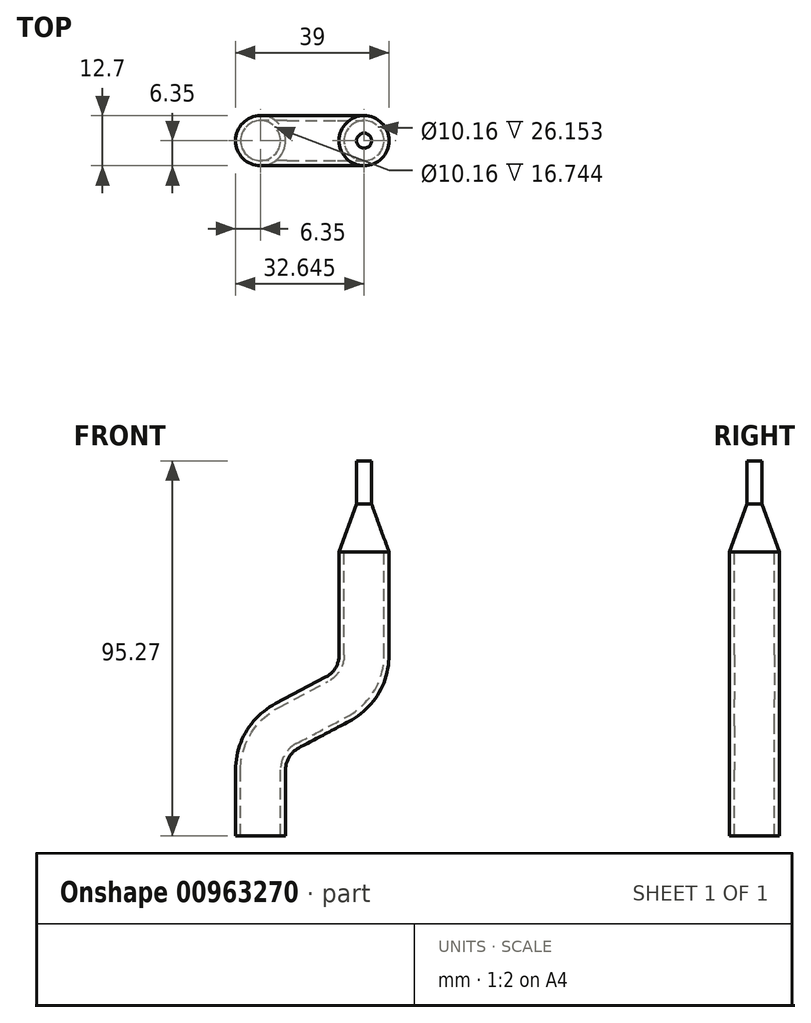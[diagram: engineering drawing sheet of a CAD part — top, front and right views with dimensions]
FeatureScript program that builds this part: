
annotation { "Feature Type Name" : "Feature", "Feature Type Description" : "" }
export const myFeature = defineFeature(function(context is Context, id is Id, definition is map)
    precondition{}
    {
        {
            var Q0;
            Q0=qCreatedBy(makeId("Front.planeOp"),FACE);
            var sketch = newSketch(context, id + "F0", { "sketchPlane" : qUnion([Q0])});
            skLineSegment(sketch, "E0", {"start": v(0, 0) * mm, "end": v(0, 18.27) * mm});
            skLineSegment(sketch, "E1", {"start": v(6.78, 29.5) * mm, "end": v(19.51, 36.21) * mm});
            skLineSegment(sketch, "E2", {"start": v(26.3, 47.45) * mm, "end": v(26.3, 73.6) * mm});
            skPoint(sketch, "E3.visualSharp", {"position": v(26.3, 39.78) * mm});
            skArc(sketch, "E3.filletArc", {"start": v(19.51, 36.21) * mm, "mid": v(24.47, 40.89) * mm, "end": v(26.3, 47.45) * mm});
            skPoint(sketch, "E4.visualSharp", {"position": v(0, 25.93) * mm});
            skArc(sketch, "E4.filletArc", {"start": v(6.78, 29.5) * mm, "mid": v(1.83, 24.83) * mm, "end": v(0, 18.27) * mm});
            skSolve(sketch);
        }
        {
            var Q0;
            Q0=qCreatedBy(makeId("Top.planeOp"),FACE);
            var sketch = newSketch(context, id + "F1", { "sketchPlane" : qUnion([Q0])});
            skCircle(sketch, "E5", {"center": v(0, 0) * mm, "radius": 6.35 * mm});
            skSolve(sketch);
        }
        {
            var Q0;
            Q0=makeQuery(id+"F1.imprint","IMPRINT",FACE,{"disambiguationData":[TD([[makeQuery(id+"F1.imprint","IMPRINT",EDGE,{"derivedFrom":sQuery(id+"F1.wireOp",EDGE,"E5")}),1.0]])]});
            var Q1;
            Q1=sQuery(id+"F0.wireOp",EDGE,"E0");
            var Q2;
            Q2=sQuery(id+"F0.wireOp",EDGE,"E4.filletArc");
            var Q3;
            Q3=sQuery(id+"F0.wireOp",EDGE,"E1");
            var Q4;
            Q4=sQuery(id+"F0.wireOp",EDGE,"E3.filletArc");
            var Q5;
            Q5=sQuery(id+"F0.wireOp",EDGE,"E2");
            sweep(context, id + "F2", {"profiles" : qUnion([Q0]), "path" : qUnion([Q1, Q2, Q3, Q4, Q5])});
        }
        {
            var Q0;
            Q0=makeQuery(id+"F2.opSweep","SWEPT_FACE",FACE,{"disambiguationData":[OSD([sQuery(id+"F0.wireOp",EDGE,"E0"),sQuery(id+"F1.wireOp",EDGE,"E5")])]});
            var Q1;
            Q1=makeQuery(id+"F2.opSweep","SWEPT_FACE",FACE,{"disambiguationData":[OSD([sQuery(id+"F0.wireOp",EDGE,"E4.filletArc"),sQuery(id+"F1.wireOp",EDGE,"E5")])]});
            var Q2;
            Q2=makeQuery(id+"F2.opSweep","SWEPT_FACE",FACE,{"disambiguationData":[OSD([sQuery(id+"F0.wireOp",EDGE,"E1"),sQuery(id+"F1.wireOp",EDGE,"E5")])]});
            var Q3;
            Q3=makeQuery(id+"F2.opSweep","SWEPT_FACE",FACE,{"disambiguationData":[OSD([sQuery(id+"F0.wireOp",EDGE,"E3.filletArc"),sQuery(id+"F1.wireOp",EDGE,"E5")])]});
            var Q4;
            Q4=makeQuery(id+"F2.opSweep","SWEPT_FACE",FACE,{"disambiguationData":[OSD([sQuery(id+"F0.wireOp",EDGE,"E2"),sQuery(id+"F1.wireOp",EDGE,"E5")])]});
            var Q5;
            Q5=makeQuery(id+"F2.opSweep","SWEPT_BODY",BODY,{"disambiguationData":[OSD([sQuery(id+"F0.wireOp",EDGE,"E2"),sQuery(id+"F1.wireOp",EDGE,"E5")])]});
            shell(context, id + "F3", {"isHollow" : true, "entities" : qUnion([Q0, Q1, Q2, Q3, Q4]), "parts" : qUnion([Q5]), "thickness" : 1.27 * mm});
        }
        {
            var Q0;
            Q0=makeQuery(id+"F2.opSweep","CAP_FACE",FACE,{"disambiguationData":[OSD([sQuery(id+"F0.wireOp",VERTEX,"E0.start"),sQuery(id+"F1.wireOp",EDGE,"E5")])],"isStart":true});
            extrude(context, id + "F4", {"entities" : qUnion([Q0]), "operationType" : NewBodyOperationType.REMOVE, "oppositeDirection" : true, "depth" : 1.52 * mm, "offsetDistance" : 25.4 * mm});
        }
        {
            var Q0;
            Q0=makeQuery(id+"F2.opSweep","CAP_FACE",FACE,{"disambiguationData":[OSD([sQuery(id+"F0.wireOp",VERTEX,"E2.end"),sQuery(id+"F1.wireOp",EDGE,"E5")])],"isStart":false});
            extrude(context, id + "F5", {"entities" : qUnion([Q0]), "operationType" : NewBodyOperationType.REMOVE, "oppositeDirection" : true, "depth" : 1.52 * mm, "offsetDistance" : 25.4 * mm});
        }
        {
            var Q0;
            Q0=makeQuery(id+"F5.boolean.opBoolean","COPY",FACE,{"derivedFrom":makeQuery(id+"F5.opExtrude","CAP_FACE",FACE,{"disambiguationData":[OSD([sQuery(id+"F0.wireOp",VERTEX,"E2.end"),sQuery(id+"F1.wireOp",EDGE,"E5")])],"isStart":false})});
            extrude(context, id + "F6", {"entities" : qUnion([Q0]), "operationType" : NewBodyOperationType.ADD, "depth" : 1.52 * mm, "offsetDistance" : 25.4 * mm});
        }
        {
            var Q0;
            Q0=qCreatedBy(makeId("Front.planeOp"),FACE);
            var sketch = newSketch(context, id + "F7", { "sketchPlane" : qUnion([Q0])});
            skLineSegment(sketch, "E6.0", {"start": v(19.95, 73.6) * mm, "end": v(32.65, 73.6) * mm});
            skPoint(sketch, "E7", {"position": v(26.3, 73.6) * mm});
            skLineSegment(sketch, "E8", {"start": v(26.3, 73.6) * mm, "end": v(26.3, 98.2) * mm, "construction": true});
            skLineSegment(sketch, "E9", {"start": v(32.65, 73.6) * mm, "end": v(28.2, 85.81) * mm});
            skLineSegment(sketch, "E10", {"start": v(28.2, 85.81) * mm, "end": v(28.2, 96.79) * mm});
            skLineSegment(sketch, "E11", {"start": v(28.2, 96.79) * mm, "end": v(26.3, 96.79) * mm});
            skLineSegment(sketch, "E12", {"start": v(26.3, 96.79) * mm, "end": v(26.3, 73.6) * mm});
            skSolve(sketch);
        }
        {
            var Q0;
            {var subQ0=sQuery(id+"F7.wireOp",EDGE,"E9");Q0=makeQuery(id+"F7.imprint","IMPRINT",FACE,{"disambiguationData":[TD([[makeQuery(id+"F7.imprint","IMPRINT",EDGE,{"derivedFrom":subQ0}),1.0]])]});}
            var Q1;
            Q1 = qConstructionFilter(qBodyType(qCreatedBy(id + "F7" ,EDGE), BodyType.WIRE), ConstructionObject.NO);
            var Q2;
            {var subQ0=sQuery(id+"F1.wireOp",EDGE,"E5");var subQ1=sQuery(id+"F0.wireOp",EDGE,"E2");Q2=makeQuery(id+"F6.boolean.opBoolean","MERGE",FACE,{"derivedFrom":[makeQuery(id+"F3.opShell","OFFSET_FACE",FACE,{"disambiguationData":[OSD([subQ1,subQ0])]}),makeQuery(id+"F6.opExtrude","SWEPT_FACE",FACE,{"disambiguationData":[OSD([sQuery(id+"F0.wireOp",VERTEX,"E2.end"),subQ1,subQ0])]})]});}
            revolve(context, id + "F8", {"surfaceOperationType" : NewSurfaceOperationType.NEW, "entities" : qUnion([Q0]), "surfaceEntities" : qUnion([Q1]), "axis" : qUnion([Q2]), "revolveType" : RevolveType.FULL});
        }
    });
